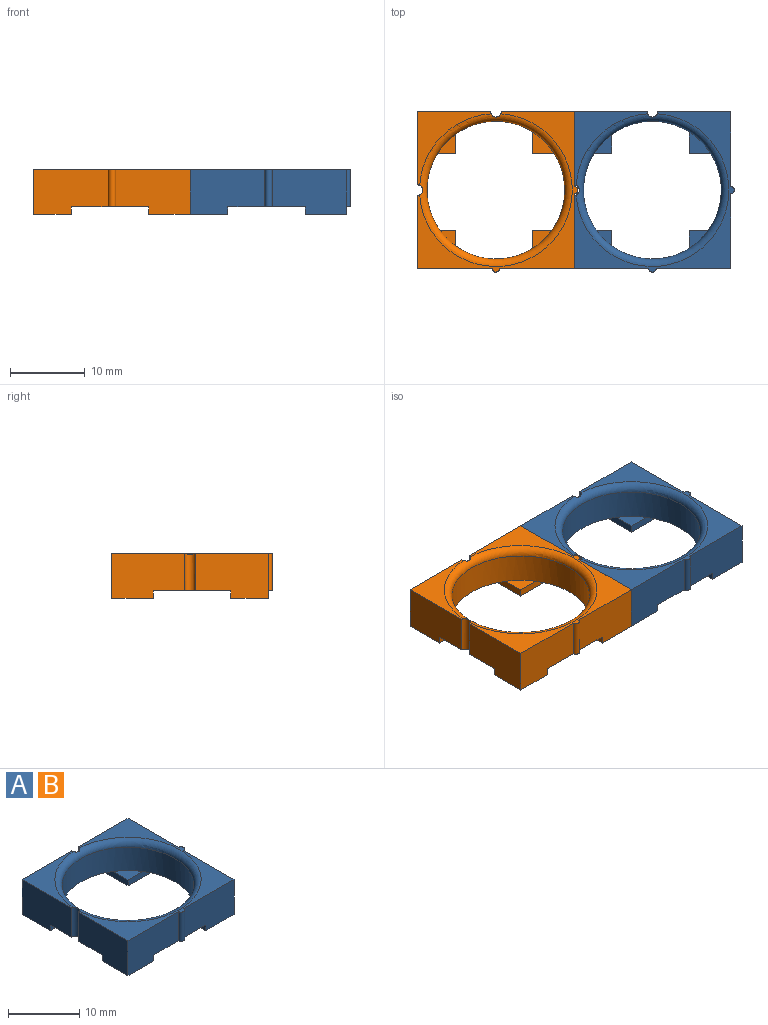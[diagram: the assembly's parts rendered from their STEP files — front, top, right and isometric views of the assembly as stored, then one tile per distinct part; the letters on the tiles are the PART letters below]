
ASSEMBLY  parts=2 mates=1
PART A: 36 faces, bbox 23.7x23.7x6 mm
  f0: plane 21.5x21.5mm, normal (0,0,1), area 83.6mm2, adj f3,f4,f9,f10,f11,f13,f31,f32
  f1: plane 9.8x6mm, normal (0,1,0), area 54.1mm2, adj f2,f5,f14,f28,f29,f33
  f2: plane 9.8x6mm, normal (-1,0,0), area 54.6mm2, adj f1,f6,f14,f27,f29,f32
  f3: plane 10x6mm, normal (1,0,0), area 55.6mm2, adj f0,f8,f11,f16,f18,f34
  f4: plane 10x6mm, normal (0,-1,0), area 55.1mm2, adj f0,f7,f13,f23,f25,f35
  f5: plane 10.4x3.03mm, normal (0,0,-1), area 17.6mm2, adj f1,f11,f12,f17,f28,f33
  f6: plane 10.4x3.03mm, normal (0,0,-1), area 17.6mm2, adj f2,f12,f13,f24,f27,f32
  f7: plane 10.4x3.53mm, normal (0,0,-1), area 18.8mm2, adj f4,f9,f12,f20,f23,f35
  f8: plane 10.4x3.53mm, normal (0,0,-1), area 18.8mm2, adj f3,f10,f12,f16,f19,f34
  f9: plane 10x6mm, normal (0,-1,0), area 55.6mm2, adj f0,f7,f10,f20,f21,f35
  f10: plane 10x6mm, normal (1,0,0), area 55.1mm2, adj f0,f8,f9,f19,f21,f34
  f11: plane 9.8x6mm, normal (0,1,0), area 54.6mm2, adj f0,f3,f5,f17,f18,f33
  f12: cylinder r=9.25mm len=18.5mm, axis (0,0,-1), area 232.5mm2, adj f5,f6,f7,f8,f15,f22,f26,f30
  f13: plane 9.8x6mm, normal (-1,0,0), area 54.1mm2, adj f0,f4,f6,f24,f25,f32
  f14: plane 9.86x9.86mm, normal (0,0,1), area 27.4mm2, adj f1,f2,f31,f32,f33
  f15: plane 2.86x2.86mm, normal (0,0,1), area 4.7mm2, adj f12,f16,f17
  f16: plane 5.55x1mm, normal (0,-1,0), area 5.6mm2, adj f3,f8,f15,f17,f18
  f17: plane 5.55x1mm, normal (-1,0,0), area 5.6mm2, adj f5,f11,f15,f16,f18
  f18: plane 5.55x5.55mm, normal (0,0,-1), area 30.8mm2, adj f3,f11,f16,f17
  f19: plane 5.55x1mm, normal (0,1,0), area 5.6mm2, adj f8,f10,f20,f21,f22
  f20: plane 5.05x1mm, normal (-1,0,0), area 5.1mm2, adj f7,f9,f19,f21,f22
  f21: plane 5.55x5.05mm, normal (0,0,-1), area 28mm2, adj f9,f10,f19,f20
  f22: plane 2.52x2.36mm, normal (0,0,1), area 3.4mm2, adj f12,f19,f20
  f23: plane 5.05x1mm, normal (1,0,0), area 5.1mm2, adj f4,f7,f24,f25,f26
  f24: plane 5.05x1mm, normal (0,1,0), area 5.1mm2, adj f6,f13,f23,f25,f26
  f25: plane 5.05x5.05mm, normal (0,0,-1), area 25.5mm2, adj f4,f13,f23,f24
  f26: plane 2.02x2.02mm, normal (0,0,1), area 2.3mm2, adj f12,f23,f24
  f27: plane 5.05x1mm, normal (0,-1,0), area 5.1mm2, adj f2,f6,f28,f29,f30
  f28: plane 5.55x1mm, normal (1,0,0), area 5.6mm2, adj f1,f5,f27,f29,f30
  f29: plane 5.55x5.05mm, normal (0,0,-1), area 28mm2, adj f1,f2,f27,f28
  f30: plane 2.52x2.36mm, normal (0,0,1), area 3.4mm2, adj f12,f27,f28
  f31: torus R=10.25mm, axis (0,0,1), area 94mm2, adj f0,f12,f14,f32,f33
  f32: cylinder r=0.7mm len=5mm, axis (0,0,1), area 10.9mm2, adj f0,f2,f6,f13,f14,f31
  f33: cylinder r=0.7mm len=5mm, axis (0,0,1), area 10.9mm2, adj f0,f1,f5,f11,f14,f31
  f34: cylinder r=0.5mm len=5mm, axis (0,0,1), area 7.9mm2, adj f0,f3,f8,f10
  f35: cylinder r=0.5mm len=5mm, axis (0,0,1), area 7.9mm2, adj f0,f4,f7,f9
PART B: same geometry as A
PLACE A t=(7.71,2.64,-2.72)mm
PLACE B t=(-13.29,2.64,-2.72)mm
MATE fastened B.f10 <-> A.f13  axis (1,0,0) through (-2.79,-7.86,-0.72)mm
